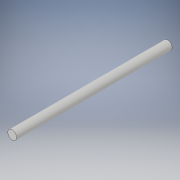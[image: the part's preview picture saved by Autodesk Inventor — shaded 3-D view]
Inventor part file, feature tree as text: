
AUTODESK INVENTOR PART (.ipt)
format: ipt  version: 2019 (Build 230136000, 136)  size: 88,064 bytes
history: native  units: in
note: dims shown in document units (in); Inventor stores cm internally (conversion verified against a paired STEP export)
features: extrude x1, sketch x1
ambient origin geometry x8: Origin, YZ Plane, XZ Plane, XY Plane, X Axis, Y Axis, Z Axis, Center Point
bodies: Solid1 (feature_tree)
feature tree (2):
  extrude  "Extrusion1"  Depth=3.3in TaperAngle=0.0deg
  sketch  "Sketch1"  dims[d0=0.188in d1=3.3in d2=0.0in d3=2.4in d4=0.0in]
